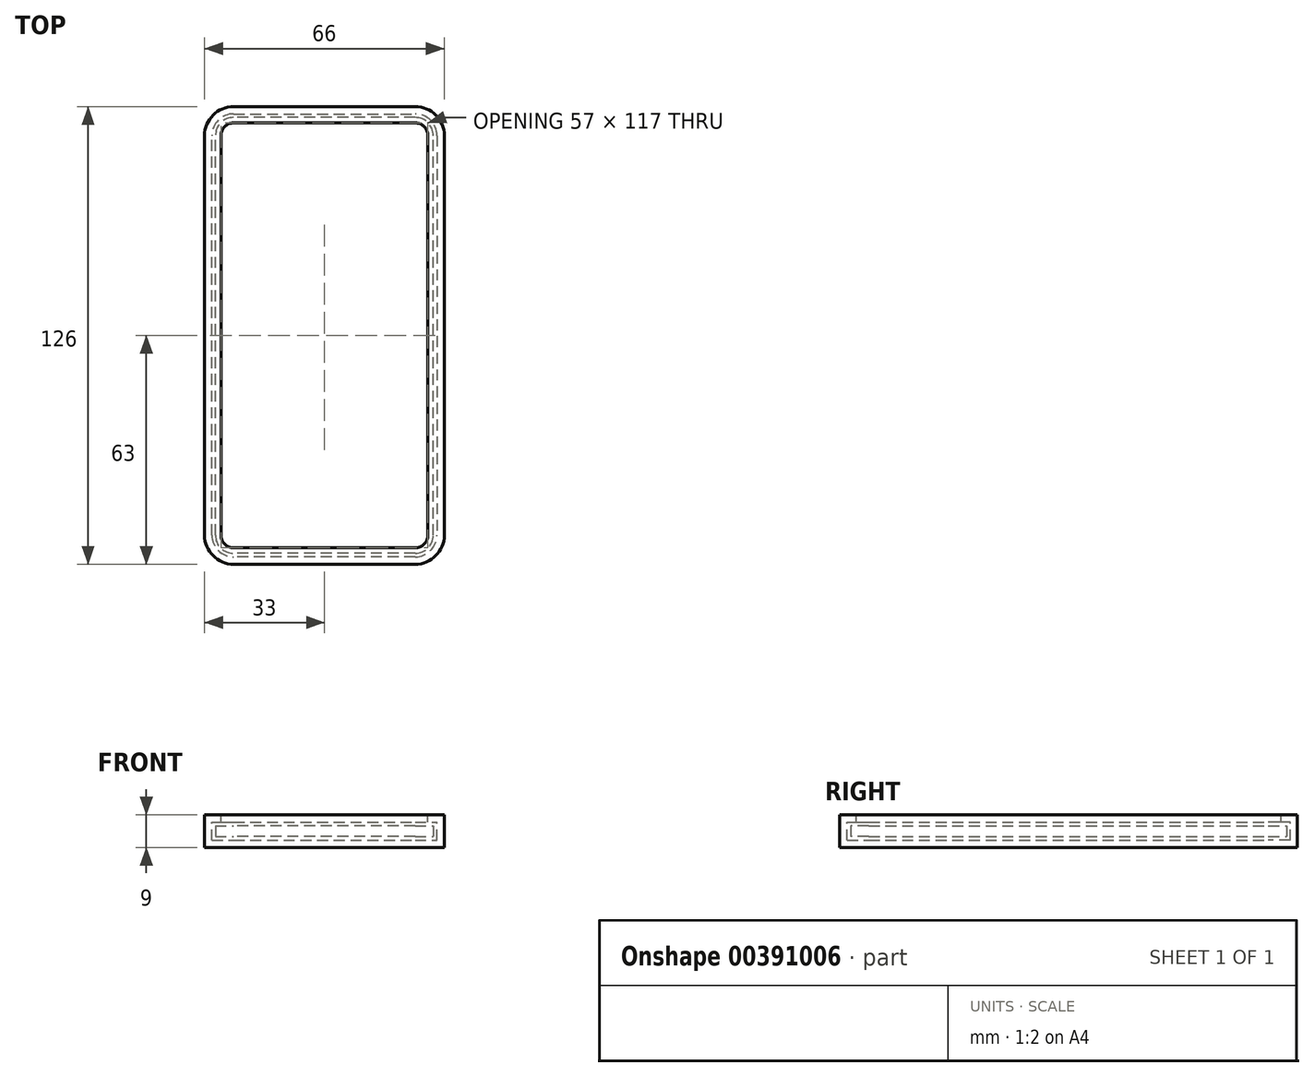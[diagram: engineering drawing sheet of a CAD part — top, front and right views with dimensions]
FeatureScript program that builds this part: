
annotation { "Feature Type Name" : "Feature", "Feature Type Description" : "" }
export const myFeature = defineFeature(function(context is Context, id is Id, definition is map)
    precondition{}
    {
        {
            assignVariable(context, id + "F0", {"name" : "epaisseurphone", "anyValue" : 3});
        }
        {
            var Q0;
            Q0=qCreatedBy(makeId("Top.planeOp"),FACE);
            var sketch = newSketch(context, id + "F1", { "sketchPlane" : qUnion([Q0])});
            skLineSegment(sketch, "E0.bottom", {"start": v(25, -60) * mm, "end": v(-25, -60) * mm});
            skLineSegment(sketch, "E0.top", {"start": v(25, 60) * mm, "end": v(-25, 60) * mm});
            skLineSegment(sketch, "E0.left", {"start": v(30, -55) * mm, "end": v(30, 55) * mm});
            skLineSegment(sketch, "E0.right", {"start": v(-30, -55) * mm, "end": v(-30, 55) * mm});
            skPoint(sketch, "E0.middle", {"position": v(0, 0) * mm});
            skPoint(sketch, "E1.visualSharp", {"position": v(30, -60) * mm});
            skArc(sketch, "E1.filletArc", {"start": v(25, -60) * mm, "mid": v(28.54, -58.54) * mm, "end": v(30, -55) * mm});
            skPoint(sketch, "E2.visualSharp", {"position": v(-30, -60) * mm});
            skArc(sketch, "E2.filletArc", {"start": v(-30, -55) * mm, "mid": v(-28.54, -58.54) * mm, "end": v(-25, -60) * mm});
            skPoint(sketch, "E3.visualSharp", {"position": v(-30, 60) * mm});
            skArc(sketch, "E3.filletArc", {"start": v(-25, 60) * mm, "mid": v(-28.54, 58.54) * mm, "end": v(-30, 55) * mm});
            skPoint(sketch, "E4.visualSharp", {"position": v(30, 60) * mm});
            skArc(sketch, "E4.filletArc", {"start": v(30, 55) * mm, "mid": v(28.54, 58.54) * mm, "end": v(25, 60) * mm});
            skArc(sketch, "E5.0", {"start": v(31, 55) * mm, "mid": v(29.24, 59.24) * mm, "end": v(25, 61) * mm});
            skLineSegment(sketch, "E5.1", {"start": v(31, -55) * mm, "end": v(31, 0) * mm});
            skLineSegment(sketch, "E5.2", {"start": v(25, 61) * mm, "end": v(-25, 61) * mm});
            skArc(sketch, "E5.3", {"start": v(25, -61) * mm, "mid": v(29.24, -59.24) * mm, "end": v(31, -55) * mm});
            skArc(sketch, "E5.4", {"start": v(-25, 61) * mm, "mid": v(-29.24, 59.24) * mm, "end": v(-31, 55) * mm});
            skLineSegment(sketch, "E5.5", {"start": v(-31, -55) * mm, "end": v(-31, 0) * mm});
            skArc(sketch, "E5.6", {"start": v(-31, -55) * mm, "mid": v(-29.24, -59.24) * mm, "end": v(-25, -61) * mm});
            skLineSegment(sketch, "E5.7", {"start": v(25, -61) * mm, "end": v(-25, -61) * mm});
            skArc(sketch, "E6.0", {"start": v(25, -63) * mm, "mid": v(30.66, -60.66) * mm, "end": v(33, -55) * mm});
            skLineSegment(sketch, "E6.1", {"start": v(25, -63) * mm, "end": v(-25, -63) * mm});
            skLineSegment(sketch, "E6.2", {"start": v(33, -55) * mm, "end": v(33, 55) * mm});
            skArc(sketch, "E6.3", {"start": v(-33, -55) * mm, "mid": v(-30.66, -60.66) * mm, "end": v(-25, -63) * mm});
            skArc(sketch, "E6.4", {"start": v(33, 55) * mm, "mid": v(30.66, 60.66) * mm, "end": v(25, 63) * mm});
            skLineSegment(sketch, "E6.5", {"start": v(25, 63) * mm, "end": v(-25, 63) * mm});
            skArc(sketch, "E6.6", {"start": v(-25, 63) * mm, "mid": v(-30.66, 60.66) * mm, "end": v(-33, 55) * mm});
            skLineSegment(sketch, "E6.7", {"start": v(-33, -55) * mm, "end": v(-33, 55) * mm});
            skLineSegment(sketch, "E7", {"start": v(-31, 0) * mm, "end": v(-31, 55) * mm});
            skLineSegment(sketch, "E8", {"start": v(31, 0) * mm, "end": v(31, 55) * mm});
            skSolve(sketch);
        }
        {
            var Q0;
            Q0=makeQuery(id+"F1.imprint","IMPRINT",FACE,{"disambiguationData":[TD([[makeQuery(id+"F1.imprint","IMPRINT",EDGE,{"derivedFrom":sQuery(id+"F1.wireOp",EDGE,"E0.bottom")}),-1.0]])]});
            extrude(context, id + "F2", {"entities" : qUnion([Q0]), "depth" : (getVariable(context, 'epaisseurphone')) * mm});
        }
        {
            var Q0;
            Q0=qCreatedBy(makeId("Front.planeOp"),FACE);
            var sketch = newSketch(context, id + "F3", { "sketchPlane" : qUnion([Q0])});
            skPoint(sketch, "E9.0", {"position": v(-31, 0) * mm});
            skPoint(sketch, "E10.0", {"position": v(-33, 0) * mm});
            skLineSegment(sketch, "E11", {"start": v(28.5, 4) * mm, "end": v(28.5, 6) * mm});
            skLineSegment(sketch, "E12", {"start": v(28.5, 6) * mm, "end": v(33, 6) * mm});
            skLineSegment(sketch, "E13", {"start": v(33, 6) * mm, "end": v(33, -3) * mm});
            skLineSegment(sketch, "E14", {"start": v(33, -3) * mm, "end": v(28.5, -3) * mm});
            skLineSegment(sketch, "E15", {"start": v(28.5, -3) * mm, "end": v(28.5, -1) * mm});
            skLineSegment(sketch, "E16", {"start": v(28.5, -1) * mm, "end": v(31, -1) * mm});
            skLineSegment(sketch, "E17", {"start": v(31, -1) * mm, "end": v(31, 4) * mm});
            skLineSegment(sketch, "E18", {"start": v(31, 4) * mm, "end": v(28.5, 4) * mm});
            skPoint(sketch, "E19.0", {"position": v(33, 0) * mm});
            skPoint(sketch, "E20.0", {"position": v(31, 0) * mm});
            skLineSegment(sketch, "E21", {"start": v(31, 4) * mm, "end": v(33, 4) * mm, "construction": true});
            skSolve(sketch);
        }
        {
            var Q0;
            Q0=makeQuery(id+"F3.imprint","IMPRINT",FACE,{"disambiguationData":[TD([[makeQuery(id+"F3.imprint","IMPRINT",EDGE,{"derivedFrom":sQuery(id+"F3.wireOp",EDGE,"E11")}),-1.0]])]});
            var Q1;
            Q1=sQuery(id+"F1.wireOp",EDGE,"E5.1");
            var Q2;
            Q2=sQuery(id+"F1.wireOp",EDGE,"E5.3");
            var Q3;
            Q3=sQuery(id+"F1.wireOp",EDGE,"E5.7");
            var Q4;
            Q4=sQuery(id+"F1.wireOp",EDGE,"E5.6");
            var Q5;
            Q5=sQuery(id+"F1.wireOp",EDGE,"E5.5");
            var Q6;
            Q6=sQuery(id+"F1.wireOp",EDGE,"E7");
            var Q7;
            Q7=sQuery(id+"F1.wireOp",EDGE,"E5.4");
            var Q8;
            Q8=sQuery(id+"F1.wireOp",EDGE,"E5.2");
            var Q9;
            Q9=sQuery(id+"F1.wireOp",EDGE,"E5.0");
            var Q10;
            Q10=sQuery(id+"F1.wireOp",EDGE,"E8");
            sweep(context, id + "F4", {"profiles" : qUnion([Q0]), "path" : qUnion([Q1, Q2, Q3, Q4, Q5, Q6, Q7, Q8, Q9, Q10])});
        }
        {
            var Q0;
            Q0=makeQuery(id+"F4.opSweep","SWEPT_FACE",FACE,{"disambiguationData":[OSD([sQuery(id+"F1.wireOp",EDGE,"E5.1"),sQuery(id+"F3.wireOp",EDGE,"E14")])]});
            var sketch = newSketch(context, id + "F5", { "sketchPlane" : qUnion([Q0])});
            skLineSegment(sketch, "E22.0", {"start": v(25, 58.5) * mm, "end": v(-25, 58.5) * mm});
            skPoint(sketch, "E23.0", {"position": v(27.47, 57.47) * mm});
            skLineSegment(sketch, "E24.0", {"start": v(28.5, -55) * mm, "end": v(28.5, 55) * mm});
            skPoint(sketch, "E25.0", {"position": v(27.47, -57.47) * mm});
            skLineSegment(sketch, "E26.0", {"start": v(-25, -58.5) * mm, "end": v(25, -58.5) * mm});
            skPoint(sketch, "E27.0", {"position": v(-27.47, -57.47) * mm});
            skArc(sketch, "E28.0", {"start": v(-28.5, -55) * mm, "mid": v(-27.47, -57.47) * mm, "end": v(-25, -58.5) * mm});
            skLineSegment(sketch, "E29.0", {"start": v(-28.5, 55) * mm, "end": v(-28.5, -55) * mm});
            skArc(sketch, "E30.0", {"start": v(-25, 58.5) * mm, "mid": v(-27.47, 57.47) * mm, "end": v(-28.5, 55) * mm});
            skArc(sketch, "E31.0", {"start": v(28.5, 55) * mm, "mid": v(27.47, 57.47) * mm, "end": v(25, 58.5) * mm});
            skArc(sketch, "E32.0", {"start": v(25, -58.5) * mm, "mid": v(27.47, -57.47) * mm, "end": v(28.5, -55) * mm});
            skSolve(sketch);
        }
        {
            var Q0;
            Q0=makeQuery(id+"F5.imprint","IMPRINT",FACE,{"disambiguationData":[TD([[makeQuery(id+"F5.imprint","IMPRINT",EDGE,{"derivedFrom":sQuery(id+"F5.wireOp",EDGE,"E22.0")}),1.0]])]});
            var Q1;
            Q1=makeQuery(id+"F4.opSweep","SWEPT_FACE",FACE,{"disambiguationData":[OSD([sQuery(id+"F1.wireOp",EDGE,"E5.1"),sQuery(id+"F3.wireOp",EDGE,"E16")])]});
            extrude(context, id + "F6", {"entities" : qUnion([Q0]), "operationType" : NewBodyOperationType.ADD, "endBound" : BoundingType.UP_TO_SURFACE, "oppositeDirection" : true, "endBoundEntityFace" : qUnion([Q1]), "depth" : 25 * mm});
        }
    });
